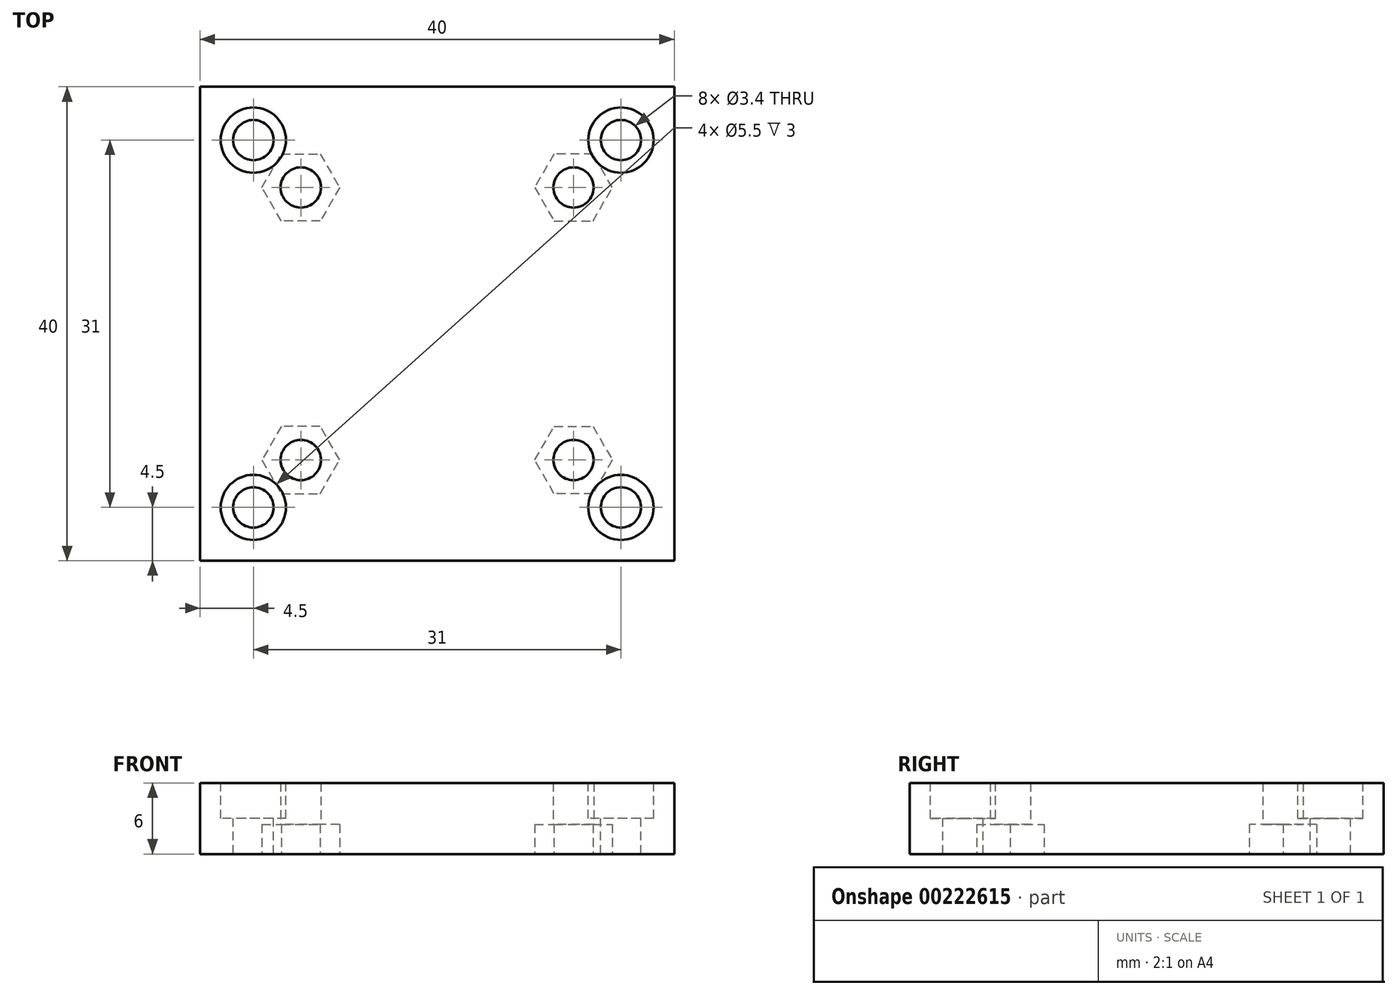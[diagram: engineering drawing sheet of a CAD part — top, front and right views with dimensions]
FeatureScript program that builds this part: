
annotation { "Feature Type Name" : "Feature", "Feature Type Description" : "" }
export const myFeature = defineFeature(function(context is Context, id is Id, definition is map)
    precondition{}
    {
        {
            var Q0;
            Q0=qCreatedBy(makeId("Top.planeOp"),FACE);
            var sketch = newSketch(context, id + "F0", { "sketchPlane" : qUnion([Q0])});
            skLineSegment(sketch, "E0.bottom", {"start": v(20, 20) * mm, "end": v(-20, 20) * mm});
            skLineSegment(sketch, "E0.top", {"start": v(20, -20) * mm, "end": v(-20, -20) * mm});
            skLineSegment(sketch, "E0.left", {"start": v(20, 20) * mm, "end": v(20, -20) * mm});
            skLineSegment(sketch, "E0.right", {"start": v(-20, 20) * mm, "end": v(-20, -20) * mm});
            skPoint(sketch, "E0.middle", {"position": v(0, 0) * mm});
            skLineSegment(sketch, "E1.bottom", {"start": v(15.5, 15.5) * mm, "end": v(-15.5, 15.5) * mm, "construction": true});
            skLineSegment(sketch, "E1.top", {"start": v(15.5, -15.5) * mm, "end": v(-15.5, -15.5) * mm, "construction": true});
            skLineSegment(sketch, "E1.left", {"start": v(15.5, 15.5) * mm, "end": v(15.5, -15.5) * mm, "construction": true});
            skLineSegment(sketch, "E1.right", {"start": v(-15.5, 15.5) * mm, "end": v(-15.5, -15.5) * mm, "construction": true});
            skLineSegment(sketch, "E2.bottom", {"start": v(11.5, 11.5) * mm, "end": v(-11.5, 11.5) * mm, "construction": true});
            skLineSegment(sketch, "E2.top", {"start": v(11.5, -11.5) * mm, "end": v(-11.5, -11.5) * mm, "construction": true});
            skLineSegment(sketch, "E2.left", {"start": v(11.5, 11.5) * mm, "end": v(11.5, -11.5) * mm, "construction": true});
            skLineSegment(sketch, "E2.right", {"start": v(-11.5, 11.5) * mm, "end": v(-11.5, -11.5) * mm, "construction": true});
            skSolve(sketch);
        }
        {
            var Q0;
            Q0=makeQuery(id+"F0.imprint","IMPRINT",FACE,{"disambiguationData":[TD([[makeQuery(id+"F0.imprint","IMPRINT",EDGE,{"derivedFrom":sQuery(id+"F0.wireOp",EDGE,"E0.bottom")}),1.0]])]});
            extrude(context, id + "F1", {"entities" : qUnion([Q0]), "depth" : 6 * mm});
        }
        {
            var Q0;
            Q0=makeQuery(id+"F1.opExtrude","CAP_FACE",FACE,{"disambiguationData":[OSD([sQuery(id+"F0.wireOp",EDGE,"E0.bottom"),sQuery(id+"F0.wireOp",EDGE,"E0.top"),sQuery(id+"F0.wireOp",EDGE,"E0.left"),sQuery(id+"F0.wireOp",EDGE,"E0.right")])],"isStart":false});
            var sketch = newSketch(context, id + "F2", { "sketchPlane" : qUnion([Q0])});
            skPoint(sketch, "E3", {"position": v(-15.5, 15.5) * mm});
            skPoint(sketch, "E4", {"position": v(15.5, 15.5) * mm});
            skPoint(sketch, "E5", {"position": v(15.5, -15.5) * mm});
            skPoint(sketch, "E6", {"position": v(-15.5, -15.5) * mm});
            skCircle(sketch, "E7.cCircle", {"center": v(-15.5, 15.5) * mm, "radius": 1.75 * mm, "construction": true});
            skLineSegment(sketch, "E7.0", {"start": v(-13.75, 15.5) * mm, "end": v(-14.26, 14.26) * mm});
            skLineSegment(sketch, "E7.1", {"start": v(-14.26, 14.26) * mm, "end": v(-15.5, 13.75) * mm});
            skLineSegment(sketch, "E7.2", {"start": v(-15.5, 13.75) * mm, "end": v(-16.74, 14.26) * mm});
            skLineSegment(sketch, "E7.3", {"start": v(-16.74, 14.26) * mm, "end": v(-17.25, 15.5) * mm});
            skLineSegment(sketch, "E7.4", {"start": v(-17.25, 15.5) * mm, "end": v(-16.74, 16.74) * mm});
            skLineSegment(sketch, "E7.5", {"start": v(-16.74, 16.74) * mm, "end": v(-15.5, 17.25) * mm});
            skLineSegment(sketch, "E7.6", {"start": v(-15.5, 17.25) * mm, "end": v(-14.26, 16.74) * mm});
            skLineSegment(sketch, "E7.7", {"start": v(-14.26, 16.74) * mm, "end": v(-13.75, 15.5) * mm});
            skSolve(sketch);
        }
        {
            var Q0;
            Q0=makeQuery(id+"F0.imprint","IMPRINT",FACE,{"disambiguationData":[TD([[makeQuery(id+"F0.imprint","IMPRINT",EDGE,{"derivedFrom":sQuery(id+"F0.wireOp",EDGE,"E0.bottom")}),1.0]])]});
            var sketch = newSketch(context, id + "F3", { "sketchPlane" : qUnion([Q0])});
            skPoint(sketch, "E8", {"position": v(-11.5, -11.5) * mm});
            skPoint(sketch, "E9", {"position": v(11.5, -11.5) * mm});
            skPoint(sketch, "E10", {"position": v(11.5, 11.5) * mm});
            skPoint(sketch, "E11", {"position": v(-11.5, 11.5) * mm});
            skCircle(sketch, "E12.cCircle", {"center": v(-11.5, 11.5) * mm, "radius": 3.28 * mm, "construction": true});
            skLineSegment(sketch, "E12.0", {"start": v(-8.23, 11.5) * mm, "end": v(-9.86, 8.66) * mm});
            skLineSegment(sketch, "E12.1", {"start": v(-9.86, 8.66) * mm, "end": v(-13.14, 8.66) * mm});
            skLineSegment(sketch, "E12.2", {"start": v(-13.14, 8.66) * mm, "end": v(-14.77, 11.5) * mm});
            skLineSegment(sketch, "E12.3", {"start": v(-14.77, 11.5) * mm, "end": v(-13.14, 14.34) * mm});
            skLineSegment(sketch, "E12.4", {"start": v(-13.14, 14.34) * mm, "end": v(-9.86, 14.34) * mm});
            skLineSegment(sketch, "E12.5", {"start": v(-9.86, 14.34) * mm, "end": v(-8.23, 11.5) * mm});
            skLineSegment(sketch, "E13.MirrorCS", {"start": v(-8.23, -11.5) * mm, "end": v(-9.86, -8.66) * mm});
            skLineSegment(sketch, "E14.MirrorCS", {"start": v(-9.86, -8.66) * mm, "end": v(-13.14, -8.66) * mm});
            skLineSegment(sketch, "E15.MirrorCS", {"start": v(-13.14, -8.66) * mm, "end": v(-14.77, -11.5) * mm});
            skLineSegment(sketch, "E16.MirrorCS", {"start": v(-14.77, -11.5) * mm, "end": v(-13.14, -14.34) * mm});
            skLineSegment(sketch, "E17.MirrorCS", {"start": v(-13.14, -14.34) * mm, "end": v(-9.86, -14.34) * mm});
            skLineSegment(sketch, "E18.MirrorCS", {"start": v(-9.86, -14.34) * mm, "end": v(-8.22, -11.5) * mm});
            skLineSegment(sketch, "E19.MirrorCS", {"start": v(9.86, -14.34) * mm, "end": v(8.22, -11.5) * mm});
            skLineSegment(sketch, "E20.MirrorCS", {"start": v(13.14, -14.34) * mm, "end": v(9.86, -14.34) * mm});
            skLineSegment(sketch, "E21.MirrorCS", {"start": v(14.77, -11.5) * mm, "end": v(13.14, -14.34) * mm});
            skLineSegment(sketch, "E22.MirrorCS", {"start": v(9.86, -8.66) * mm, "end": v(13.14, -8.66) * mm});
            skLineSegment(sketch, "E23.MirrorCS", {"start": v(8.22, -11.5) * mm, "end": v(9.86, -8.66) * mm});
            skLineSegment(sketch, "E24.MirrorCS", {"start": v(13.14, -8.66) * mm, "end": v(14.77, -11.5) * mm});
            skLineSegment(sketch, "E25.MirrorCS", {"start": v(9.86, 8.66) * mm, "end": v(13.14, 8.66) * mm});
            skLineSegment(sketch, "E26.MirrorCS", {"start": v(8.22, 11.5) * mm, "end": v(9.86, 8.66) * mm});
            skLineSegment(sketch, "E27.MirrorCS", {"start": v(9.86, 14.34) * mm, "end": v(8.22, 11.5) * mm});
            skLineSegment(sketch, "E28.MirrorCS", {"start": v(13.14, 14.34) * mm, "end": v(9.86, 14.34) * mm});
            skLineSegment(sketch, "E29.MirrorCS", {"start": v(14.77, 11.5) * mm, "end": v(13.14, 14.34) * mm});
            skLineSegment(sketch, "E30.MirrorCS", {"start": v(13.14, 8.66) * mm, "end": v(14.77, 11.5) * mm});
            skSolve(sketch);
        }
        {
            var Q0;
            Q0=sQuery(id+"F2.wireOp",VERTEX,"E3");
            var Q1;
            Q1=sQuery(id+"F2.wireOp",VERTEX,"E4");
            var Q2;
            Q2=sQuery(id+"F2.wireOp",VERTEX,"E5");
            var Q3;
            Q3=sQuery(id+"F2.wireOp",VERTEX,"E6");
            var Q4;
            Q4=makeQuery(id+"F1.opExtrude","SWEPT_BODY",BODY,{"disambiguationData":[OSD([sQuery(id+"F0.wireOp",EDGE,"E0.bottom"),sQuery(id+"F0.wireOp",EDGE,"E0.top"),sQuery(id+"F0.wireOp",EDGE,"E0.left"),sQuery(id+"F0.wireOp",EDGE,"E0.right")])]});
            hole(context, id + "F4", {"style" : HoleStyle.C_BORE, "endStyle" : HoleEndStyle.THROUGH, "holeDiameter" : 3.4 * mm, "cBoreDiameter" : 5.5 * mm, "cBoreDepth" : 3 * mm, "startFromSketch" : true, "locations" : qUnion([Q0, Q1, Q2, Q3]), "scope" : qUnion([Q4]), "isTappedThrough" : true});
        }
        {
            var Q0;
            Q0=sQuery(id+"F3.wireOp",VERTEX,"E8");
            var Q1;
            Q1=sQuery(id+"F3.wireOp",VERTEX,"E9");
            var Q2;
            Q2=sQuery(id+"F3.wireOp",VERTEX,"E10");
            var Q3;
            Q3=sQuery(id+"F3.wireOp",VERTEX,"E11");
            var Q4;
            Q4=makeQuery(id+"F1.opExtrude","SWEPT_BODY",BODY,{"disambiguationData":[OSD([sQuery(id+"F0.wireOp",EDGE,"E0.bottom"),sQuery(id+"F0.wireOp",EDGE,"E0.top"),sQuery(id+"F0.wireOp",EDGE,"E0.left"),sQuery(id+"F0.wireOp",EDGE,"E0.right")])]});
            hole(context, id + "F5", {"style" : HoleStyle.SIMPLE, "endStyle" : HoleEndStyle.THROUGH, "oppositeDirection" : true, "holeDiameter" : 3.4 * mm, "startFromSketch" : true, "locations" : qUnion([Q0, Q1, Q2, Q3]), "scope" : qUnion([Q4]), "isTappedThrough" : true});
        }
        {
            var Q0;
            Q0=makeQuery(id+"F3.imprint","IMPRINT",FACE,{"disambiguationData":[TD([[makeQuery(id+"F3.imprint","IMPRINT",EDGE,{"derivedFrom":sQuery(id+"F3.wireOp",EDGE,"E12.0")}),-1.0]])]});
            var Q1;
            Q1=makeQuery(id+"F3.imprint","IMPRINT",FACE,{"disambiguationData":[TD([[makeQuery(id+"F3.imprint","IMPRINT",EDGE,{"derivedFrom":sQuery(id+"F3.wireOp",EDGE,"E13.MirrorCS")}),1.0]])]});
            var Q2;
            Q2=makeQuery(id+"F3.imprint","IMPRINT",FACE,{"disambiguationData":[TD([[makeQuery(id+"F3.imprint","IMPRINT",EDGE,{"derivedFrom":sQuery(id+"F3.wireOp",EDGE,"E20.MirrorCS")}),-1.0]])]});
            var Q3;
            Q3=makeQuery(id+"F3.imprint","IMPRINT",FACE,{"disambiguationData":[TD([[makeQuery(id+"F3.imprint","IMPRINT",EDGE,{"derivedFrom":sQuery(id+"F3.wireOp",EDGE,"E25.MirrorCS")}),1.0]])]});
            extrude(context, id + "F6", {"entities" : qUnion([Q0, Q1, Q2, Q3]), "operationType" : NewBodyOperationType.REMOVE, "depth" : 2.5 * mm});
        }
    });
